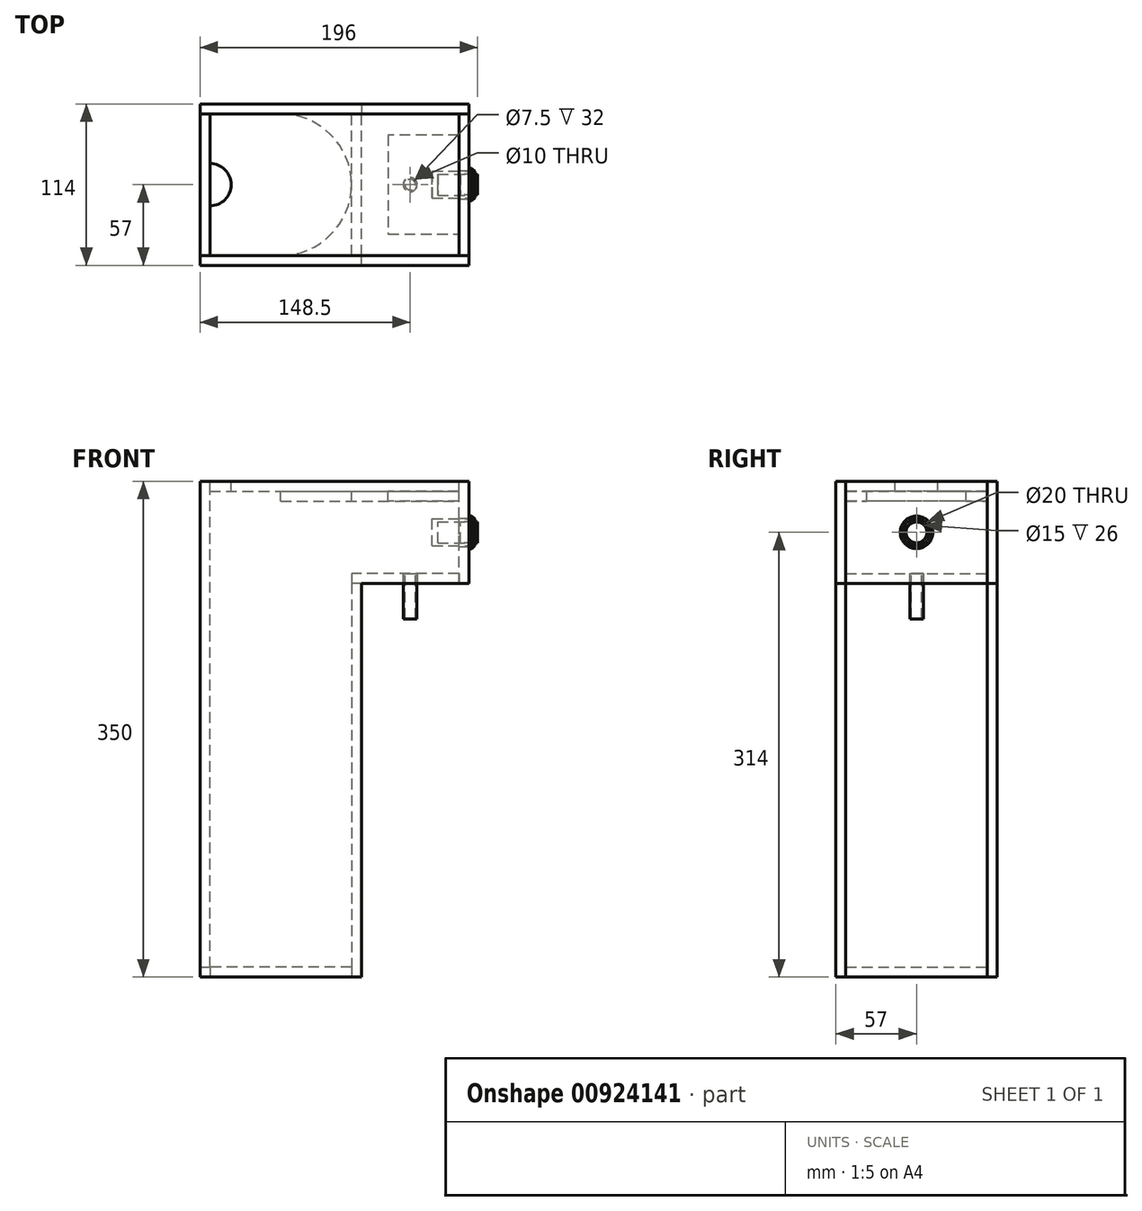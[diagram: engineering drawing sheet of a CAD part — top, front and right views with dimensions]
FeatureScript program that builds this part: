
annotation { "Feature Type Name" : "Feature", "Feature Type Description" : "" }
export const myFeature = defineFeature(function(context is Context, id is Id, definition is map)
    precondition{}
    {
        {
            var Q0;
            Q0=qCreatedBy(makeId("Top.planeOp"),FACE);
            var sketch = newSketch(context, id + "F0", { "sketchPlane" : qUnion([Q0])});
            skLineSegment(sketch, "E0.bottom", {"start": v(50, -50) * mm, "end": v(-50, -50) * mm});
            skLineSegment(sketch, "E0.top", {"start": v(50, 50) * mm, "end": v(-50, 50) * mm});
            skLineSegment(sketch, "E0.left", {"start": v(50, -50) * mm, "end": v(50, 50) * mm});
            skLineSegment(sketch, "E0.right", {"start": v(-50, -50) * mm, "end": v(-50, 50) * mm});
            skSolve(sketch);
        }
        {
            var Q0;
            Q0=makeQuery(id+"F0.imprint","IMPRINT",FACE,{"disambiguationData":[TD([[makeQuery(id+"F0.imprint","IMPRINT",EDGE,{"derivedFrom":sQuery(id+"F0.wireOp",EDGE,"E0.bottom")}),-1.0]])]});
            extrude(context, id + "F1", {"entities" : qUnion([Q0]), "depth" : 7 * mm, "offsetDistance" : 25 * mm});
        }
        {
            var Q0;
            Q0=makeQuery(id+"F1.opExtrude","SWEPT_FACE",FACE,{"disambiguationData":[OSD([sQuery(id+"F0.wireOp",EDGE,"E0.top")])]});
            var sketch = newSketch(context, id + "F2", { "sketchPlane" : qUnion([Q0])});
            skLineSegment(sketch, "E1", {"start": v(-57, 0) * mm, "end": v(-57, 278) * mm});
            skLineSegment(sketch, "E2", {"start": v(-57, 278) * mm, "end": v(-133, 278) * mm});
            skLineSegment(sketch, "E3", {"start": v(-133, 278) * mm, "end": v(-133, 350) * mm});
            skLineSegment(sketch, "E4", {"start": v(-133, 350) * mm, "end": v(57, 350) * mm});
            skLineSegment(sketch, "E5", {"start": v(57, 350) * mm, "end": v(57, 0) * mm});
            skLineSegment(sketch, "E6", {"start": v(57, 0) * mm, "end": v(-57, 0) * mm});
            skSolve(sketch);
        }
        {
            var Q0;
            Q0 = qSketchRegion(id + "F2", true);
            extrude(context, id + "F3", {"entities" : qUnion([Q0]), "depth" : 7 * mm, "offsetDistance" : 25 * mm});
        }
        {
            var Q0;
            Q0 = qSketchRegion(id + "F2", true);
            extrude(context, id + "F4", {"entities" : qUnion([Q0]), "oppositeDirection" : true, "depth" : 107 * mm, "offsetDistance" : 25 * mm, "hasSecondDirection" : true, "secondDirectionOppositeDirection" : false, "secondDirectionDepth" : -100 * mm});
        }
        {
            var Q0;
            Q0=makeQuery(id+"F1.opExtrude","SWEPT_FACE",FACE,{"disambiguationData":[OSD([sQuery(id+"F0.wireOp",EDGE,"E0.left")])]});
            var sketch = newSketch(context, id + "F5", { "sketchPlane" : qUnion([Q0])});
            skLineSegment(sketch, "E7.bottom", {"start": v(-50, 0) * mm, "end": v(50, 0) * mm});
            skLineSegment(sketch, "E7.top", {"start": v(-50, 278) * mm, "end": v(50, 278) * mm});
            skLineSegment(sketch, "E7.left", {"start": v(-50, 0) * mm, "end": v(-50, 278) * mm});
            skLineSegment(sketch, "E7.right", {"start": v(50, 0) * mm, "end": v(50, 278) * mm});
            skSolve(sketch);
        }
        {
            var Q0;
            Q0 = qSketchRegion(id + "F5", true);
            extrude(context, id + "F6", {"entities" : qUnion([Q0]), "depth" : 7 * mm, "offsetDistance" : 25 * mm});
        }
        {
            var Q0;
            Q0=makeQuery(id+"F1.opExtrude","SWEPT_FACE",FACE,{"disambiguationData":[OSD([sQuery(id+"F0.wireOp",EDGE,"E0.right")])]});
            var sketch = newSketch(context, id + "F7", { "sketchPlane" : qUnion([Q0])});
            skLineSegment(sketch, "E8.bottom", {"start": v(-50, 0) * mm, "end": v(50, 0) * mm});
            skLineSegment(sketch, "E8.top", {"start": v(-50, 350) * mm, "end": v(50, 350) * mm});
            skLineSegment(sketch, "E8.left", {"start": v(-50, 0) * mm, "end": v(-50, 350) * mm});
            skLineSegment(sketch, "E8.right", {"start": v(50, 0) * mm, "end": v(50, 350) * mm});
            skSolve(sketch);
        }
        {
            var Q0;
            {var subQ0=sQuery(id+"F7.wireOp",EDGE,"E8.top");Q0=makeQuery(id+"F7.imprint","IMPRINT",FACE,{"disambiguationData":[TD([[makeQuery(id+"F7.imprint","IMPRINT",EDGE,{"derivedFrom":subQ0}),-1.0]])]});}
            extrude(context, id + "F8", {"entities" : qUnion([Q0]), "depth" : 7 * mm, "offsetDistance" : 25 * mm});
        }
        {
            var Q0;
            Q0=makeQuery(id+"F4.opExtrude","SWEPT_FACE",FACE,{"disambiguationData":[OSD([sQuery(id+"F2.wireOp",EDGE,"E3")])]});
            var sketch = newSketch(context, id + "F9", { "sketchPlane" : qUnion([Q0])});
            skLineSegment(sketch, "E9.bottom", {"start": v(-50, 350) * mm, "end": v(50, 350) * mm});
            skLineSegment(sketch, "E9.top", {"start": v(-50, 278) * mm, "end": v(50, 278) * mm});
            skLineSegment(sketch, "E9.left", {"start": v(-50, 350) * mm, "end": v(-50, 278) * mm});
            skLineSegment(sketch, "E9.right", {"start": v(50, 350) * mm, "end": v(50, 278) * mm});
            skCircle(sketch, "E10", {"center": v(0, 314) * mm, "radius": 10 * mm});
            skLineSegment(sketch, "E11", {"start": v(0, 350) * mm, "end": v(0, 278) * mm, "construction": true});
            skSolve(sketch);
        }
        {
            var Q0;
            Q0 = qSketchRegion(id + "F9", true);
            extrude(context, id + "F10", {"entities" : qUnion([Q0]), "depth" : -7 * mm, "offsetDistance" : 25 * mm});
        }
        {
            var Q0;
            Q0=makeQuery(id+"F3.opExtrude","SWEPT_FACE",FACE,{"disambiguationData":[OSD([sQuery(id+"F2.wireOp",EDGE,"E4")])]});
            var sketch = newSketch(context, id + "F11", { "sketchPlane" : qUnion([Q0])});
            skLineSegment(sketch, "E12.bottom", {"start": v(-50, -50) * mm, "end": v(126, -50) * mm});
            skLineSegment(sketch, "E12.top", {"start": v(-50, 50) * mm, "end": v(126, 50) * mm});
            skLineSegment(sketch, "E12.left", {"start": v(-50, -50) * mm, "end": v(-50, 50) * mm});
            skLineSegment(sketch, "E12.right", {"start": v(126, -50) * mm, "end": v(126, 50) * mm});
            skCircle(sketch, "E13", {"center": v(-50, 0) * mm, "radius": 15 * mm});
            skSolve(sketch);
        }
        {
            var Q0;
            {var subQ4=sQuery(id+"F11.wireOp",EDGE,"E12.bottom");Q0=makeQuery(id+"F11.imprint","IMPRINT",FACE,{"disambiguationData":[TD([[makeQuery(id+"F11.imprint","IMPRINT",EDGE,{"derivedFrom":subQ4}),1.0]])]});}
            extrude(context, id + "F12", {"entities" : qUnion([Q0]), "depth" : -7 * mm, "offsetDistance" : 25 * mm});
        }
        {
            var Q0;
            Q0=makeQuery(id+"F10.opExtrude","SWEPT_FACE",FACE,{"disambiguationData":[OSD([sQuery(id+"F9.wireOp",EDGE,"E9.top")])]});
            var sketch = newSketch(context, id + "F13", { "sketchPlane" : qUnion([Q0])});
            skLineSegment(sketch, "E14.bottom", {"start": v(126, 50) * mm, "end": v(50, 50) * mm});
            skLineSegment(sketch, "E14.top", {"start": v(126, -50) * mm, "end": v(50, -50) * mm});
            skLineSegment(sketch, "E14.left", {"start": v(126, 50) * mm, "end": v(126, -50) * mm});
            skLineSegment(sketch, "E14.right", {"start": v(50, 50) * mm, "end": v(50, -50) * mm});
            skLineSegment(sketch, "E15", {"start": v(126, 0) * mm, "end": v(57, 0) * mm, "construction": true});
            skLineSegment(sketch, "E16", {"start": v(57, 0) * mm, "end": v(50, 0) * mm, "construction": true});
            skCircle(sketch, "E17", {"center": v(91.5, 0) * mm, "radius": 5 * mm});
            skSolve(sketch);
        }
        {
            var Q0;
            Q0 = qSketchRegion(id + "F13", true);
            extrude(context, id + "F14", {"entities" : qUnion([Q0]), "depth" : -7 * mm, "offsetDistance" : 25 * mm});
        }
        {
            var Q0;
            Q0=qCreatedBy(makeId("Front.planeOp"),FACE);
            var sketch = newSketch(context, id + "F15", { "sketchPlane" : qUnion([Q0])});
            skLineSegment(sketch, "E18", {"start": v(133, 323.5) * mm, "end": v(133, 325.5) * mm});
            skLineSegment(sketch, "E19", {"start": v(133, 325.5) * mm, "end": v(135, 325.5) * mm});
            skLineSegment(sketch, "E20", {"start": v(135, 325.5) * mm, "end": v(137, 323.5) * mm});
            skLineSegment(sketch, "E21", {"start": v(137, 323.5) * mm, "end": v(137, 321.5) * mm});
            skLineSegment(sketch, "E22", {"start": v(137, 321.5) * mm, "end": v(111, 321.5) * mm});
            skLineSegment(sketch, "E23", {"start": v(111, 321.5) * mm, "end": v(111, 314) * mm});
            skLineSegment(sketch, "E24", {"start": v(111, 314) * mm, "end": v(107, 314) * mm});
            skLineSegment(sketch, "E25", {"start": v(107, 314) * mm, "end": v(107, 323.5) * mm});
            skLineSegment(sketch, "E26", {"start": v(107, 323.5) * mm, "end": v(133, 323.5) * mm});
            skSolve(sketch);
        }
        {
            var Q0;
            Q0 = qSketchRegion(id + "F15", true);
            var Q1;
            Q1=sQuery(id+"F15.wireOp",EDGE,"E24");
            revolve(context, id + "F16", {"surfaceOperationType" : NewSurfaceOperationType.NEW, "entities" : qUnion([Q0]), "axis" : qUnion([Q1]), "revolveType" : RevolveType.FULL});
        }
        {
            var Q0;
            Q0=makeQuery(id+"F16.opRevolve","SWEPT_FACE",FACE,{"disambiguationData":[OSD([sQuery(id+"F15.wireOp",EDGE,"E21")])]});
            var sketch = newSketch(context, id + "F17", { "sketchPlane" : qUnion([Q0])});
            skCircle(sketch, "E27", {"center": v(0, 314) * mm, "radius": 7.4 * mm});
            skSolve(sketch);
        }
        {
            var Q0;
            Q0 = qSketchRegion(id + "F17", true);
            extrude(context, id + "F18", {"entities" : qUnion([Q0]), "depth" : 2 * mm, "offsetDistance" : 25 * mm, "hasSecondDirection" : true, "secondDirectionOppositeDirection" : true, "secondDirectionDepth" : 10 * mm});
        }
        {
            var Q0;
            Q0=makeQuery(id+"F14.opExtrude","CAP_FACE",FACE,{"disambiguationData":[OSD([sQuery(id+"F13.wireOp",EDGE,"E14.bottom"),sQuery(id+"F13.wireOp",EDGE,"E14.top"),sQuery(id+"F13.wireOp",EDGE,"E14.left"),sQuery(id+"F13.wireOp",EDGE,"E14.right"),sQuery(id+"F13.wireOp",EDGE,"E17")])],"isStart":true});
            var sketch = newSketch(context, id + "F19", { "sketchPlane" : qUnion([Q0])});
            skCircle(sketch, "E28", {"center": v(91.5, 0) * mm, "radius": 4.75 * mm});
            skCircle(sketch, "E29", {"center": v(91.5, 0) * mm, "radius": 3.75 * mm});
            skSolve(sketch);
        }
        {
            var Q0;
            Q0 = qSketchRegion(id + "F19", true);
            extrude(context, id + "F20", {"entities" : qUnion([Q0]), "depth" : 25 * mm, "offsetDistance" : 25 * mm, "hasSecondDirection" : true, "secondDirectionOppositeDirection" : true, "secondDirectionDepth" : 7 * mm});
        }
        {
            var Q0;
            Q0=makeQuery(id+"F12.opExtrude","CAP_FACE",FACE,{"disambiguationData":[OSD([sQuery(id+"F11.wireOp",EDGE,"E12.bottom"),sQuery(id+"F11.wireOp",EDGE,"E12.top"),sQuery(id+"F11.wireOp",EDGE,"E12.left"),sQuery(id+"F11.wireOp",EDGE,"E12.right"),sQuery(id+"F11.wireOp",EDGE,"E13")])],"isStart":false});
            var sketch = newSketch(context, id + "F21", { "sketchPlane" : qUnion([Q0])});
            skLineSegment(sketch, "E30", {"start": v(-50, -50) * mm, "end": v(50, 50) * mm, "construction": true});
            skCircle(sketch, "E31", {"center": v(0, 0) * mm, "radius": 50 * mm});
            skLineSegment(sketch, "E32", {"start": v(126, -35) * mm, "end": v(76, -35) * mm});
            skLineSegment(sketch, "E33", {"start": v(76, -35) * mm, "end": v(76, 35) * mm});
            skLineSegment(sketch, "E34", {"start": v(76, 35) * mm, "end": v(126, 35) * mm});
            skLineSegment(sketch, "E35", {"start": v(0, -50) * mm, "end": v(126, -50) * mm});
            skLineSegment(sketch, "E36", {"start": v(126, -50) * mm, "end": v(126, -35) * mm});
            skLineSegment(sketch, "E37", {"start": v(126, 35) * mm, "end": v(126, 50) * mm});
            skLineSegment(sketch, "E38", {"start": v(126, 50) * mm, "end": v(3.15, 50) * mm});
            skSolve(sketch);
        }
        {
            var Q0;
            Q0=makeQuery(id+"F21.imprint","IMPRINT",FACE,{"disambiguationData":[TD([[makeQuery(id+"F21.imprint","IMPRINT",EDGE,{"derivedFrom":sQuery(id+"F21.wireOp",EDGE,"E32")}),1.0]])]});
            extrude(context, id + "F22", {"entities" : qUnion([Q0]), "depth" : 7 * mm, "offsetDistance" : 25 * mm});
        }
    });
